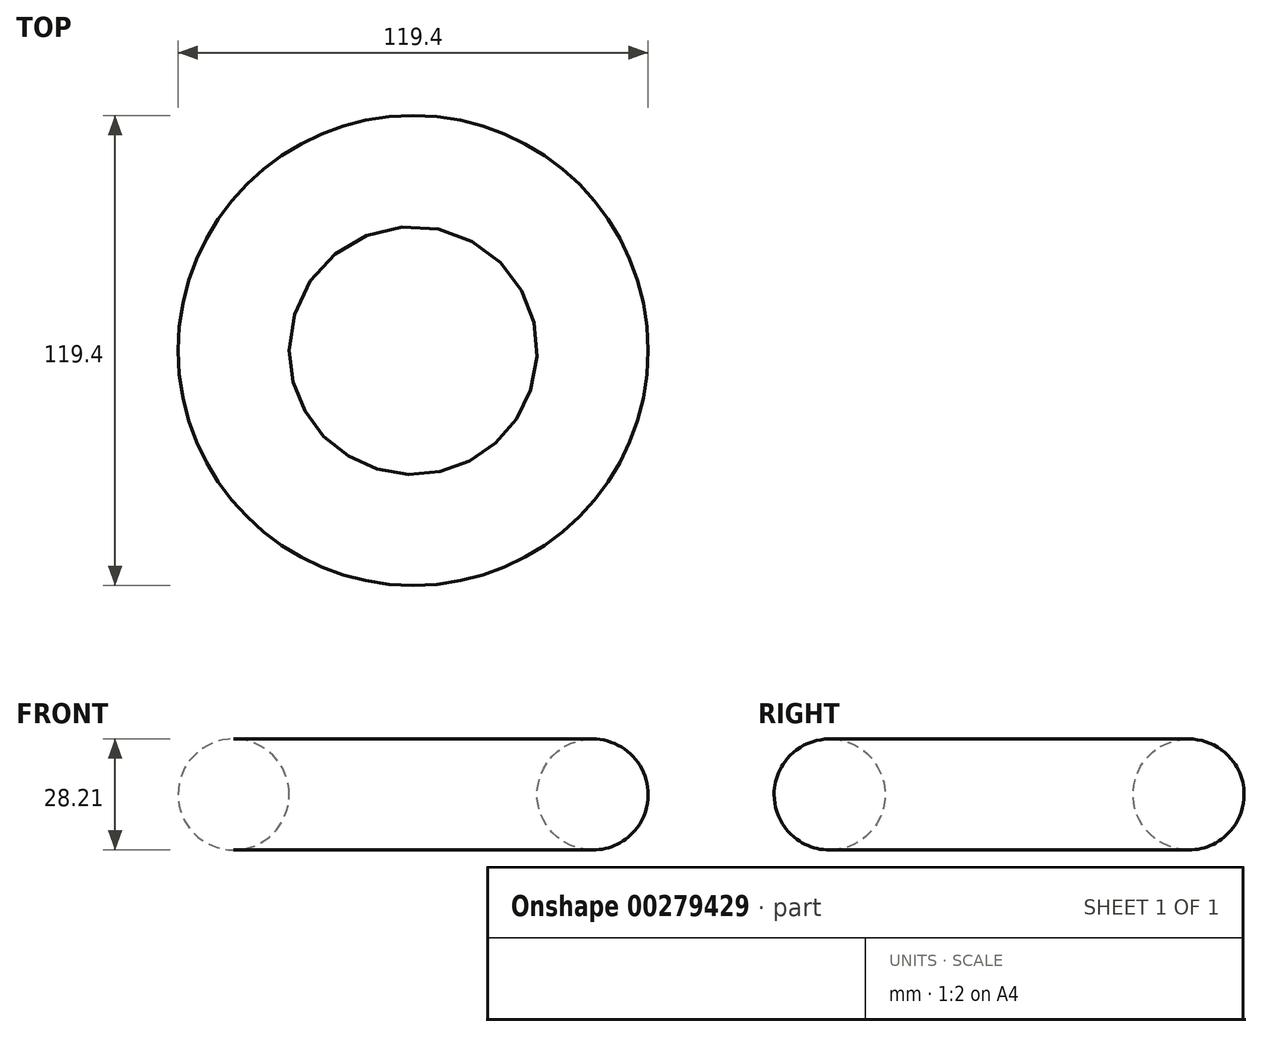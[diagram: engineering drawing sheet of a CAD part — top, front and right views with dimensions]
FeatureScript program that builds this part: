
annotation { "Feature Type Name" : "Feature", "Feature Type Description" : "" }
export const myFeature = defineFeature(function(context is Context, id is Id, definition is map)
    precondition{}
    {
        {
            var Q0;
            Q0=qCreatedBy(makeId("Front.planeOp"),FACE);
            var sketch = newSketch(context, id + "F0", { "sketchPlane" : qUnion([Q0])});
            skLineSegment(sketch, "E0", {"start": v(0, 0) * mm, "end": v(0, 22.7) * mm});
            skCircle(sketch, "E1", {"center": v(45.6, 20.15) * mm, "radius": 14.1 * mm});
            skSolve(sketch);
        }
        {
            var Q0;
            Q0=makeQuery(id+"F0.imprint","IMPRINT",FACE,{"disambiguationData":[TD([[makeQuery(id+"F0.imprint","IMPRINT",EDGE,{"derivedFrom":sQuery(id+"F0.wireOp",EDGE,"E1")}),1.0]])]});
            var Q1;
            Q1=sQuery(id+"F0.wireOp",EDGE,"E0");
            revolve(context, id + "F1", {"entities" : qUnion([Q0]), "axis" : qUnion([Q1]), "revolveType" : RevolveType.FULL});
        }
    });
